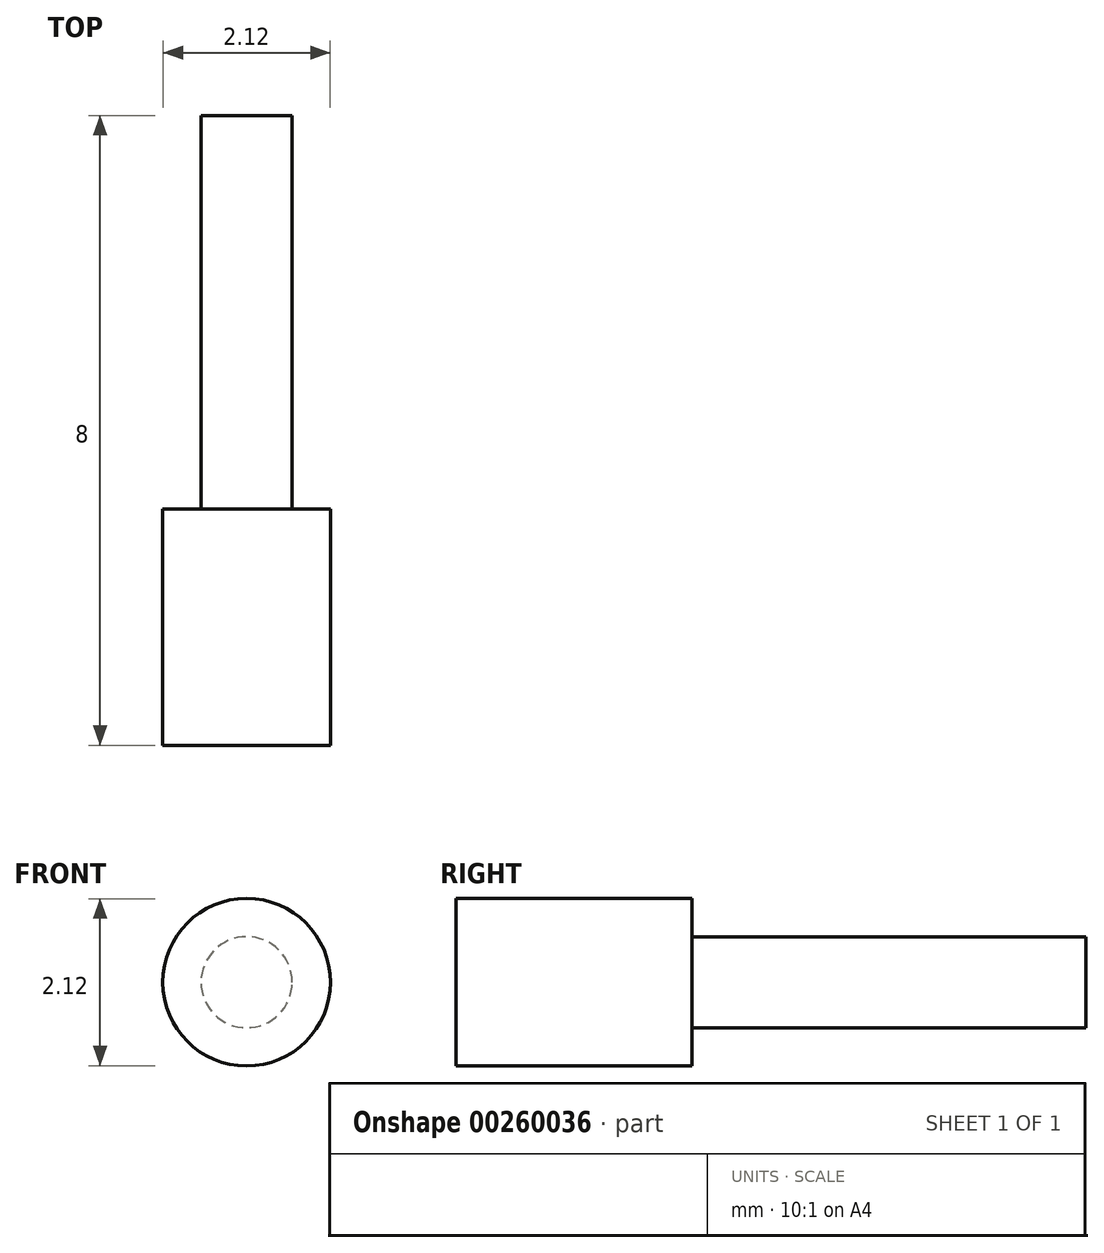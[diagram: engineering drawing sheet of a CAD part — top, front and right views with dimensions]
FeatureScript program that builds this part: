
annotation { "Feature Type Name" : "Feature", "Feature Type Description" : "" }
export const myFeature = defineFeature(function(context is Context, id is Id, definition is map)
    precondition{}
    {
        {
            var Q0;
            Q0=qCreatedBy(makeId("Front.planeOp"),FACE);
            var sketch = newSketch(context, id + "F0", { "sketchPlane" : qUnion([Q0])});
            skCircle(sketch, "E0", {"center": v(0, 0) * mm, "radius": 0.58 * mm});
            skSolve(sketch);
        }
        {
            var Q0;
            Q0=qSketchRegion(id+"F0",true);
            extrude(context, id + "F1", {"entities" : qUnion([Q0]), "endBound" : BoundingType.SYMMETRIC, "depth" : 5 * mm});
        }
        {
            var Q0;
            Q0=makeQuery(id+"F1.opExtrude","CAP_FACE",FACE,{"disambiguationData":[OSD([sQuery(id+"F0.wireOp",EDGE,"E0")])],"isStart":false});
            var sketch = newSketch(context, id + "F2", { "sketchPlane" : qUnion([Q0])});
            skCircle(sketch, "E1", {"center": v(0, 0) * mm, "radius": 1.06 * mm});
            skSolve(sketch);
        }
        {
            var Q0;
            Q0=qSketchRegion(id+"F2",true);
            extrude(context, id + "F3", {"entities" : qUnion([Q0]), "operationType" : NewBodyOperationType.ADD, "depth" : 3 * mm});
        }
    });
